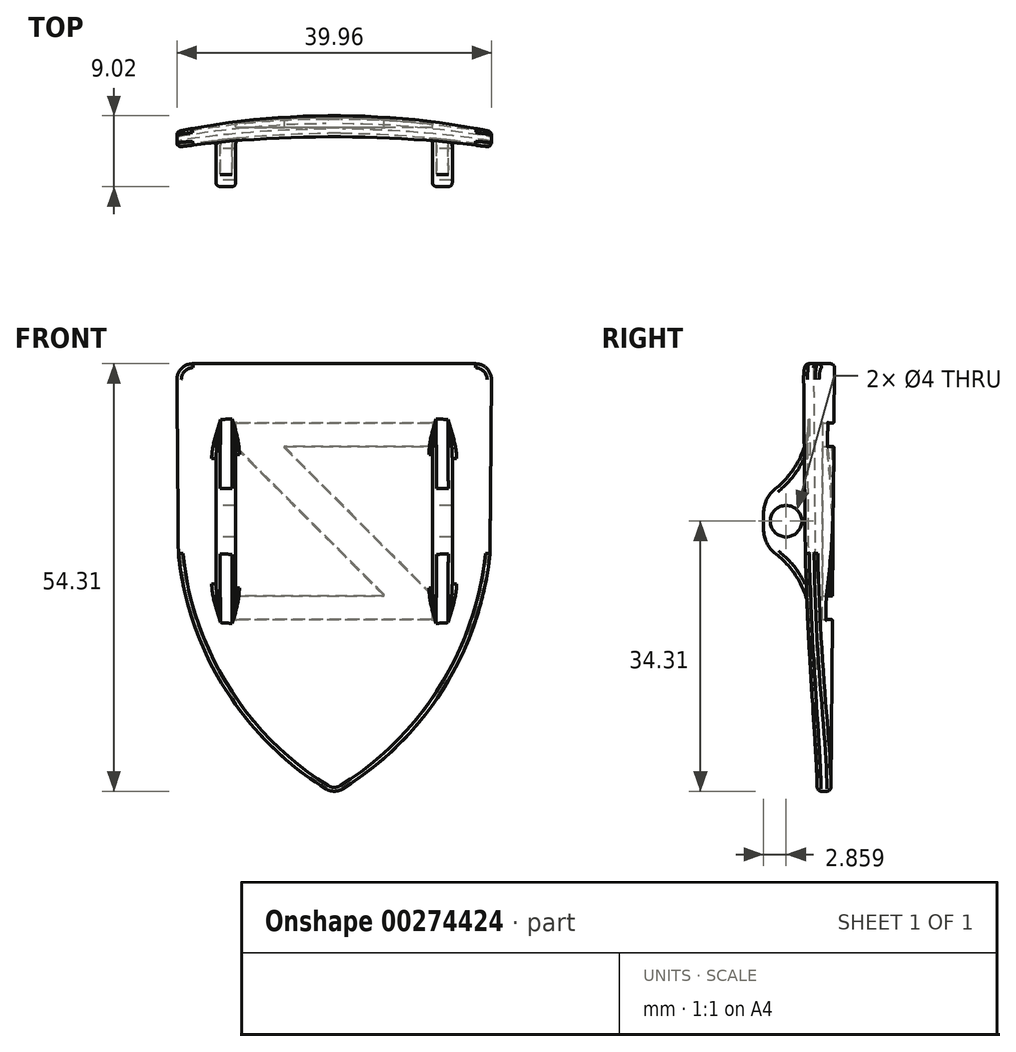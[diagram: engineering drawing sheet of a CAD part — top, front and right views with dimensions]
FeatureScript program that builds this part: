
annotation { "Feature Type Name" : "Feature", "Feature Type Description" : "" }
export const myFeature = defineFeature(function(context is Context, id is Id, definition is map)
    precondition{}
    {
        {
            var Q0;
            Q0=qCreatedBy(makeId("Top.planeOp"),FACE);
            var sketch = newSketch(context, id + "F0", { "sketchPlane" : qUnion([Q0])});
            skLineSegment(sketch, "E0", {"start": v(0, 0) * mm, "end": v(-20, 0) * mm});
            skLineSegment(sketch, "E1", {"start": v(0, 0) * mm, "end": v(20, 0) * mm});
            skArc(sketch, "E2", {"start": v(20, 0) * mm, "mid": v(0, 2.02) * mm, "end": v(-20, 0) * mm});
            skLineSegment(sketch, "E3", {"start": v(-20, 0) * mm, "end": v(-20, -2) * mm});
            skLineSegment(sketch, "E4", {"start": v(20, 0) * mm, "end": v(20, -2) * mm});
            skArc(sketch, "E5", {"start": v(20, -2) * mm, "mid": v(0, -0.66) * mm, "end": v(-20, -2) * mm});
            skSolve(sketch);
        }
        {
            var Q0;
            Q0=qCreatedBy(makeId("Front.planeOp"),FACE);
            var sketch = newSketch(context, id + "F1", { "sketchPlane" : qUnion([Q0])});
            skPoint(sketch, "E6.0", {"position": v(-20, 0) * mm});
            skPoint(sketch, "E7.0", {"position": v(20, 0) * mm});
            skLineSegment(sketch, "E8.bottom", {"start": v(-20, 0) * mm, "end": v(20, 0) * mm});
            skLineSegment(sketch, "E8.top", {"start": v(-20, -60) * mm, "end": v(20, -60) * mm});
            skLineSegment(sketch, "E8.left", {"start": v(-20, 0) * mm, "end": v(-20, -60) * mm});
            skLineSegment(sketch, "E8.right", {"start": v(20, 0) * mm, "end": v(20, -60) * mm});
            skPoint(sketch, "E9", {"position": v(-20, -20) * mm});
            skArc(sketch, "E10", {"start": v(20, -20) * mm, "mid": v(14.64, -40) * mm, "end": v(0, -54.64) * mm});
            skArc(sketch, "E11", {"start": v(-20, -20) * mm, "mid": v(-14.64, -40) * mm, "end": v(0, -54.64) * mm});
            skLineSegment(sketch, "E12.bottom", {"start": v(-12.5, -25) * mm, "end": v(12.5, -25) * mm});
            skLineSegment(sketch, "E12.top", {"start": v(-12.5, -15) * mm, "end": v(12.5, -15) * mm});
            skLineSegment(sketch, "E12.left", {"start": v(-12.5, -25) * mm, "end": v(-12.5, -15) * mm});
            skLineSegment(sketch, "E12.right", {"start": v(12.5, -25) * mm, "end": v(12.5, -15) * mm});
            skPoint(sketch, "E12.middle", {"position": v(0, -20) * mm});
            skLineSegment(sketch, "E13.bottom", {"start": v(-12.5, -25) * mm, "end": v(-15, -25) * mm});
            skLineSegment(sketch, "E13.top", {"start": v(-12.5, -15) * mm, "end": v(-15, -15) * mm});
            skLineSegment(sketch, "E13.right", {"start": v(-15, -25) * mm, "end": v(-15, -15) * mm});
            skLineSegment(sketch, "E14.MirrorCS", {"start": v(12.5, -15) * mm, "end": v(15, -15) * mm});
            skLineSegment(sketch, "E15.MirrorCS", {"start": v(15, -25) * mm, "end": v(15, -15) * mm});
            skLineSegment(sketch, "E16.MirrorCS", {"start": v(12.5, -25) * mm, "end": v(15, -25) * mm});
            skSolve(sketch);
        }
        {
            var Q0;
            Q0=makeQuery(id+"F0.imprint","IMPRINT",FACE,{"disambiguationData":[TD([[makeQuery(id+"F0.imprint","IMPRINT",EDGE,{"derivedFrom":sQuery(id+"F0.wireOp",EDGE,"E0")}),1.0]])]});
            var Q1;
            Q1=makeQuery(id+"F0.imprint","IMPRINT",FACE,{"disambiguationData":[TD([[makeQuery(id+"F0.imprint","IMPRINT",EDGE,{"derivedFrom":sQuery(id+"F0.wireOp",EDGE,"E0")}),-1.0]])]});
            extrude(context, id + "F2", {"entities" : qUnion([Q0, Q1]), "oppositeDirection" : true, "depth" : 60 * mm, "hasDraft" : true, "draftAngle" : 0.5 * degree, "draftPullDirection" : true});
        }
        {
            var Q0;
            {var subQ2=sQuery(id+"F1.wireOp",EDGE,"E8.top");Q0=makeQuery(id+"F1.imprint","IMPRINT",FACE,{"disambiguationData":[TD([[makeQuery(id+"F1.imprint","IMPRINT",EDGE,{"derivedFrom":subQ2}),1.0]])]});}
            extrude(context, id + "F3", {"entities" : qUnion([Q0]), "operationType" : NewBodyOperationType.REMOVE, "endBound" : BoundingType.SYMMETRIC, "depth" : 5 * mm});
        }
        {
            var Q0;
            Q0=makeQuery(id+"F1.imprint","IMPRINT",FACE,{"disambiguationData":[TD([[makeQuery(id+"F1.imprint","IMPRINT",EDGE,{"derivedFrom":sQuery(id+"F1.wireOp",EDGE,"E13.bottom")}),-1.0]])]});
            var Q1;
            Q1=makeQuery(id+"F1.imprint","IMPRINT",FACE,{"disambiguationData":[TD([[makeQuery(id+"F1.imprint","IMPRINT",EDGE,{"derivedFrom":sQuery(id+"F1.wireOp",EDGE,"E12.right")}),-1.0]])]});
            extrude(context, id + "F4", {"entities" : qUnion([Q0, Q1]), "operationType" : NewBodyOperationType.ADD, "depth" : 7 * mm});
        }
        {
            var Q0;
            Q0=makeQuery(id+"F4.opExtrude","SWEPT_FACE",FACE,{"disambiguationData":[OSD([sQuery(id+"F1.wireOp",EDGE,"E13.right")])]});
            var sketch = newSketch(context, id + "F5", { "sketchPlane" : qUnion([Q0])});
            skCircle(sketch, "E17", {"center": v(4.14, -20) * mm, "radius": 2 * mm});
            skPoint(sketch, "E17.centerSnap0", {"position": v(4.14, -15) * mm});
            skPoint(sketch, "E17.centerSnap1", {"position": v(7, -20) * mm});
            skSolve(sketch);
        }
        {
            var Q0;
            Q0=makeQuery(id+"F5.imprint","IMPRINT",FACE,{"disambiguationData":[TD([[makeQuery(id+"F5.imprint","IMPRINT",EDGE,{"derivedFrom":sQuery(id+"F5.wireOp",EDGE,"E17")}),1.0]])]});
            extrude(context, id + "F6", {"entities" : qUnion([Q0]), "operationType" : NewBodyOperationType.REMOVE, "oppositeDirection" : true, "depth" : 30 * mm});
        }
        {
            var Q0;
            Q0=makeQuery(id+"F4.opExtrude","CAP_EDGE",EDGE,{"disambiguationData":[OSD([sQuery(id+"F1.wireOp",EDGE,"E13.top")])],"isStart":false});
            var Q1;
            Q1=makeQuery(id+"F4.opExtrude","CAP_EDGE",EDGE,{"disambiguationData":[OSD([sQuery(id+"F1.wireOp",EDGE,"E13.bottom")])],"isStart":false});
            var Q2;
            Q2=makeQuery(id+"F4.opExtrude","CAP_EDGE",EDGE,{"disambiguationData":[OSD([sQuery(id+"F1.wireOp",EDGE,"E14.MirrorCS")])],"isStart":false});
            var Q3;
            Q3=makeQuery(id+"F4.opExtrude","CAP_EDGE",EDGE,{"disambiguationData":[OSD([sQuery(id+"F1.wireOp",EDGE,"E16.MirrorCS")])],"isStart":false});
            fillet(context, id + "F7", {"entities" : qUnion([Q0, Q1, Q2, Q3]), "radius" : 4 * mm, "tangentPropagation" : true, "allowEdgeOverflow" : false});
        }
        {
            var Q0;
            Q0=makeQuery(id+"F2.opExtrude","SWEPT_FACE",FACE,{"disambiguationData":[OSD([sQuery(id+"F0.wireOp",EDGE,"E2")])]});
            var Q1;
            Q1=makeQuery(id+"F2.opExtrude","CAP_EDGE",EDGE,{"disambiguationData":[OSD([sQuery(id+"F0.wireOp",EDGE,"E5")])],"isStart":true});
            var Q2;
            Q2=makeQuery(id+"F2.opExtrude","SWEPT_EDGE",EDGE,{"disambiguationData":[OSD([sQuery(id+"F0.wireOp",EDGE,"E3"),sQuery(id+"F0.wireOp",EDGE,"E5")])]});
            var Q3;
            Q3=makeQuery(id+"F3.boolean.opBoolean","INTERSECT",EDGE,{"derivedFrom":[makeQuery(id+"F2.opExtrude","SWEPT_FACE",FACE,{"disambiguationData":[OSD([sQuery(id+"F0.wireOp",EDGE,"E5")])]}),makeQuery(id+"F3.opExtrude","SWEPT_FACE",FACE,{"disambiguationData":[OSD([sQuery(id+"F1.wireOp",EDGE,"E11")])]})]});
            var Q4;
            Q4=makeQuery(id+"F2.opExtrude","SWEPT_EDGE",EDGE,{"disambiguationData":[OSD([sQuery(id+"F0.wireOp",EDGE,"E4"),sQuery(id+"F0.wireOp",EDGE,"E5")])]});
            var Q5;
            Q5=makeQuery(id+"F3.boolean.opBoolean","INTERSECT",EDGE,{"derivedFrom":[makeQuery(id+"F2.opExtrude","SWEPT_FACE",FACE,{"disambiguationData":[OSD([sQuery(id+"F0.wireOp",EDGE,"E5")])]}),makeQuery(id+"F3.opExtrude","SWEPT_FACE",FACE,{"disambiguationData":[OSD([sQuery(id+"F1.wireOp",EDGE,"E10")])]})]});
            fillet(context, id + "F8", {"entities" : qUnion([Q0, Q1, Q2, Q3, Q4, Q5]), "radius" : 0.5 * mm, "tangentPropagation" : true, "allowEdgeOverflow" : false});
        }
        {
            var Q0;
            Q0=makeQuery(id+"F2.opExtrude","CAP_EDGE",EDGE,{"disambiguationData":[OSD([sQuery(id+"F0.wireOp",EDGE,"E3")])],"isStart":true});
            var Q1;
            Q1=makeQuery(id+"F3.boolean.opBoolean","COPY",EDGE,{"derivedFrom":makeQuery(id+"F3.opExtrude","SWEPT_EDGE",EDGE,{"disambiguationData":[OSD([sQuery(id+"F1.wireOp",EDGE,"E10"),sQuery(id+"F1.wireOp",EDGE,"E11")])]})});
            var Q2;
            Q2=makeQuery(id+"F2.opExtrude","CAP_EDGE",EDGE,{"disambiguationData":[OSD([sQuery(id+"F0.wireOp",EDGE,"E4")])],"isStart":true});
            var Q3;
            Q3=makeQuery(id+"F3.boolean.opBoolean","INTERSECT",EDGE,{"derivedFrom":[makeQuery(id+"F2.opExtrude","SWEPT_FACE",FACE,{"disambiguationData":[OSD([sQuery(id+"F0.wireOp",EDGE,"E3")])]}),makeQuery(id+"F3.opExtrude","SWEPT_FACE",FACE,{"disambiguationData":[OSD([sQuery(id+"F1.wireOp",EDGE,"E11")])]})]});
            var Q4;
            Q4=makeQuery(id+"F3.boolean.opBoolean","INTERSECT",EDGE,{"derivedFrom":[makeQuery(id+"F2.opExtrude","SWEPT_FACE",FACE,{"disambiguationData":[OSD([sQuery(id+"F0.wireOp",EDGE,"E4")])]}),makeQuery(id+"F3.opExtrude","SWEPT_FACE",FACE,{"disambiguationData":[OSD([sQuery(id+"F1.wireOp",EDGE,"E10")])]})]});
            fillet(context, id + "F9", {"entities" : qUnion([Q0, Q1, Q2, Q3, Q4]), "radius" : 2 * mm, "tangentPropagation" : true, "allowEdgeOverflow" : false});
        }
        {
            var Q0;
            Q0=makeQuery(id+"F6.boolean.opBoolean","COPY",FACE,{"disambiguationData":[TD([makeQuery(id+"F4.opExtrude","SWEPT_FACE",FACE,{"disambiguationData":[OSD([sQuery(id+"F1.wireOp",EDGE,"E12.left")])]})])],"derivedFrom":makeQuery(id+"F6.opExtrude","SWEPT_FACE",FACE,{"disambiguationData":[OSD([sQuery(id+"F5.wireOp",EDGE,"E17")])]})});
            var Q1;
            Q1=makeQuery(id+"F6.boolean.opBoolean","COPY",FACE,{"disambiguationData":[TD([makeQuery(id+"F4.opExtrude","SWEPT_FACE",FACE,{"disambiguationData":[OSD([sQuery(id+"F1.wireOp",EDGE,"E12.right")])]})])],"derivedFrom":makeQuery(id+"F6.opExtrude","SWEPT_FACE",FACE,{"disambiguationData":[OSD([sQuery(id+"F5.wireOp",EDGE,"E17")])]})});
            fillet(context, id + "F10", {"entities" : qUnion([Q0, Q1]), "radius" : 0.1 * mm, "tangentPropagation" : true, "allowEdgeOverflow" : false});
        }
        {
            var Q0;
            Q0=qCreatedBy(makeId("Front.planeOp"),FACE);
            cPlane(context, id + "F11", {"entities" : qUnion([Q0]), "cplaneType" : CPlaneType.OFFSET, "offset" : 10 * mm, "oppositeDirection" : true, "width" : 150 * mm, "height" : 150 * mm});
        }
        {
            var Q0;
            Q0=qCreatedBy(id+"F11.planeOp",FACE);
            var sketch = newSketch(context, id + "F12", { "sketchPlane" : qUnion([Q0])});
            skPoint(sketch, "E18.0", {"position": v(0, -20) * mm});
            skPoint(sketch, "E19.0", {"position": v(-12.5, -15) * mm});
            skPoint(sketch, "E20.0", {"position": v(12.5, -15) * mm});
            skLineSegment(sketch, "E21.bottom", {"start": v(-12.5, -7.5) * mm, "end": v(12.5, -7.5) * mm, "construction": true});
            skLineSegment(sketch, "E21.top", {"start": v(-12.5, -32.5) * mm, "end": v(12.5, -32.5) * mm, "construction": true});
            skLineSegment(sketch, "E21.left", {"start": v(-12.5, -7.5) * mm, "end": v(-12.5, -32.5) * mm, "construction": true});
            skLineSegment(sketch, "E21.right", {"start": v(12.5, -7.5) * mm, "end": v(12.5, -32.5) * mm, "construction": true});
            skLineSegment(sketch, "E22", {"start": v(9.5, -29.5) * mm, "end": v(-9.5, -10.5) * mm, "construction": true});
            skLineSegment(sketch, "E23.bottom", {"start": v(12.5, -7.5) * mm, "end": v(-12.5, -7.5) * mm});
            skLineSegment(sketch, "E23.top", {"start": v(12.5, -10.5) * mm, "end": v(-6.5, -10.5) * mm});
            skLineSegment(sketch, "E23.left", {"start": v(12.5, -7.5) * mm, "end": v(12.5, -10.5) * mm});
            skLineSegment(sketch, "E23.right", {"start": v(-12.5, -7.5) * mm, "end": v(-12.5, -10.5) * mm});
            skLineSegment(sketch, "E24.bottom", {"start": v(12.5, -32.5) * mm, "end": v(-12.5, -32.5) * mm});
            skLineSegment(sketch, "E24.left", {"start": v(12.5, -32.5) * mm, "end": v(12.5, -29.5) * mm});
            skLineSegment(sketch, "E24.right", {"start": v(-12.5, -32.5) * mm, "end": v(-12.5, -29.5) * mm});
            skLineSegment(sketch, "E25", {"start": v(12.5, -29.5) * mm, "end": v(-6.5, -10.5) * mm});
            skLineSegment(sketch, "E26", {"start": v(-12.5, -10.5) * mm, "end": v(6.5, -29.5) * mm});
            skLineSegment(sketch, "E27.trimOffspring", {"start": v(6.5, -29.5) * mm, "end": v(-12.5, -29.5) * mm});
            skSolve(sketch);
        }
        {
            var Q0;
            Q0=makeQuery(id+"F12.imprint","IMPRINT",FACE,{"disambiguationData":[TD([[makeQuery(id+"F12.imprint","IMPRINT",EDGE,{"derivedFrom":sQuery(id+"F12.wireOp",EDGE,"E23.bottom")}),1.0]])]});
            extrude(context, id + "F13", {"entities" : qUnion([Q0]), "operationType" : NewBodyOperationType.REMOVE, "depth" : 9.5 * mm});
        }
        {
            var Q0;
            Q0=makeQuery(id+"F13.boolean.opBoolean","INTERSECT",EDGE,{"derivedFrom":[makeQuery(id+"F2.opExtrude","SWEPT_FACE",FACE,{"disambiguationData":[OSD([sQuery(id+"F0.wireOp",EDGE,"E2")])]}),makeQuery(id+"F13.opExtrude","SWEPT_FACE",FACE,{"disambiguationData":[OSD([sQuery(id+"F12.wireOp",EDGE,"E23.top")])]})]});
            var Q1;
            Q1=makeQuery(id+"F13.boolean.opBoolean","INTERSECT",EDGE,{"derivedFrom":[makeQuery(id+"F2.opExtrude","SWEPT_FACE",FACE,{"disambiguationData":[OSD([sQuery(id+"F0.wireOp",EDGE,"E2")])]}),makeQuery(id+"F13.opExtrude","SWEPT_FACE",FACE,{"disambiguationData":[OSD([sQuery(id+"F12.wireOp",EDGE,"E23.left")])]})]});
            var Q2;
            Q2=makeQuery(id+"F13.boolean.opBoolean","INTERSECT",EDGE,{"derivedFrom":[makeQuery(id+"F2.opExtrude","SWEPT_FACE",FACE,{"disambiguationData":[OSD([sQuery(id+"F0.wireOp",EDGE,"E2")])]}),makeQuery(id+"F13.opExtrude","SWEPT_FACE",FACE,{"disambiguationData":[OSD([sQuery(id+"F12.wireOp",EDGE,"E23.bottom")])]})]});
            var Q3;
            Q3=makeQuery(id+"F13.boolean.opBoolean","INTERSECT",EDGE,{"derivedFrom":[makeQuery(id+"F2.opExtrude","SWEPT_FACE",FACE,{"disambiguationData":[OSD([sQuery(id+"F0.wireOp",EDGE,"E2")])]}),makeQuery(id+"F13.opExtrude","SWEPT_FACE",FACE,{"disambiguationData":[OSD([sQuery(id+"F12.wireOp",EDGE,"E23.right")])]})]});
            var Q4;
            Q4=makeQuery(id+"F13.boolean.opBoolean","INTERSECT",EDGE,{"derivedFrom":[makeQuery(id+"F2.opExtrude","SWEPT_FACE",FACE,{"disambiguationData":[OSD([sQuery(id+"F0.wireOp",EDGE,"E2")])]}),makeQuery(id+"F13.opExtrude","SWEPT_FACE",FACE,{"disambiguationData":[OSD([sQuery(id+"F12.wireOp",EDGE,"E26")])]})]});
            var Q5;
            Q5=makeQuery(id+"F13.boolean.opBoolean","INTERSECT",EDGE,{"derivedFrom":[makeQuery(id+"F2.opExtrude","SWEPT_FACE",FACE,{"disambiguationData":[OSD([sQuery(id+"F0.wireOp",EDGE,"E2")])]}),makeQuery(id+"F13.opExtrude","SWEPT_FACE",FACE,{"disambiguationData":[OSD([sQuery(id+"F12.wireOp",EDGE,"E27.trimOffspring")])]})]});
            var Q6;
            Q6=makeQuery(id+"F13.boolean.opBoolean","INTERSECT",EDGE,{"derivedFrom":[makeQuery(id+"F2.opExtrude","SWEPT_FACE",FACE,{"disambiguationData":[OSD([sQuery(id+"F0.wireOp",EDGE,"E2")])]}),makeQuery(id+"F13.opExtrude","SWEPT_FACE",FACE,{"disambiguationData":[OSD([sQuery(id+"F12.wireOp",EDGE,"E24.bottom")])]})]});
            var Q7;
            Q7=makeQuery(id+"F13.boolean.opBoolean","INTERSECT",EDGE,{"derivedFrom":[makeQuery(id+"F2.opExtrude","SWEPT_FACE",FACE,{"disambiguationData":[OSD([sQuery(id+"F0.wireOp",EDGE,"E2")])]}),makeQuery(id+"F13.opExtrude","SWEPT_FACE",FACE,{"disambiguationData":[OSD([sQuery(id+"F12.wireOp",EDGE,"E24.right")])]})]});
            var Q8;
            Q8=makeQuery(id+"F13.boolean.opBoolean","INTERSECT",EDGE,{"derivedFrom":[makeQuery(id+"F2.opExtrude","SWEPT_FACE",FACE,{"disambiguationData":[OSD([sQuery(id+"F0.wireOp",EDGE,"E2")])]}),makeQuery(id+"F13.opExtrude","SWEPT_FACE",FACE,{"disambiguationData":[OSD([sQuery(id+"F12.wireOp",EDGE,"E24.left")])]})]});
            var Q9;
            Q9=makeQuery(id+"F13.boolean.opBoolean","INTERSECT",EDGE,{"derivedFrom":[makeQuery(id+"F2.opExtrude","SWEPT_FACE",FACE,{"disambiguationData":[OSD([sQuery(id+"F0.wireOp",EDGE,"E2")])]}),makeQuery(id+"F13.opExtrude","SWEPT_FACE",FACE,{"disambiguationData":[OSD([sQuery(id+"F12.wireOp",EDGE,"E25")])]})]});
            var Q10;
            Q10=makeQuery(id+"F13.boolean.opBoolean","COPY",EDGE,{"derivedFrom":makeQuery(id+"F13.opExtrude","SWEPT_EDGE",EDGE,{"disambiguationData":[OSD([sQuery(id+"F12.wireOp",EDGE,"E23.top"),sQuery(id+"F12.wireOp",EDGE,"E25")])]})});
            var Q11;
            Q11=makeQuery(id+"F13.boolean.opBoolean","COPY",EDGE,{"derivedFrom":makeQuery(id+"F13.opExtrude","SWEPT_EDGE",EDGE,{"disambiguationData":[OSD([sQuery(id+"F12.wireOp",EDGE,"E26"),sQuery(id+"F12.wireOp",EDGE,"E27.trimOffspring")])]})});
            var Q12;
            Q12=makeQuery(id+"F13.boolean.opBoolean","COPY",EDGE,{"derivedFrom":makeQuery(id+"F13.opExtrude","SWEPT_EDGE",EDGE,{"disambiguationData":[OSD([sQuery(id+"F12.wireOp",EDGE,"E23.bottom"),sQuery(id+"F12.wireOp",EDGE,"E23.right")])]})});
            var Q13;
            Q13=makeQuery(id+"F13.boolean.opBoolean","COPY",EDGE,{"derivedFrom":makeQuery(id+"F13.opExtrude","SWEPT_EDGE",EDGE,{"disambiguationData":[OSD([sQuery(id+"F12.wireOp",EDGE,"E23.right"),sQuery(id+"F12.wireOp",EDGE,"E26")])]})});
            var Q14;
            Q14=makeQuery(id+"F13.boolean.opBoolean","COPY",EDGE,{"derivedFrom":makeQuery(id+"F13.opExtrude","SWEPT_EDGE",EDGE,{"disambiguationData":[OSD([sQuery(id+"F12.wireOp",EDGE,"E23.top"),sQuery(id+"F12.wireOp",EDGE,"E23.left")])]})});
            var Q15;
            Q15=makeQuery(id+"F13.boolean.opBoolean","COPY",EDGE,{"derivedFrom":makeQuery(id+"F13.opExtrude","SWEPT_EDGE",EDGE,{"disambiguationData":[OSD([sQuery(id+"F12.wireOp",EDGE,"E23.bottom"),sQuery(id+"F12.wireOp",EDGE,"E23.left")])]})});
            var Q16;
            Q16=makeQuery(id+"F13.boolean.opBoolean","COPY",EDGE,{"derivedFrom":makeQuery(id+"F13.opExtrude","SWEPT_EDGE",EDGE,{"disambiguationData":[OSD([sQuery(id+"F12.wireOp",EDGE,"E24.bottom"),sQuery(id+"F12.wireOp",EDGE,"E24.left")])]})});
            var Q17;
            Q17=makeQuery(id+"F13.boolean.opBoolean","COPY",EDGE,{"derivedFrom":makeQuery(id+"F13.opExtrude","SWEPT_EDGE",EDGE,{"disambiguationData":[OSD([sQuery(id+"F12.wireOp",EDGE,"E24.left"),sQuery(id+"F12.wireOp",EDGE,"E25")])]})});
            var Q18;
            Q18=makeQuery(id+"F13.boolean.opBoolean","COPY",EDGE,{"derivedFrom":makeQuery(id+"F13.opExtrude","SWEPT_EDGE",EDGE,{"disambiguationData":[OSD([sQuery(id+"F12.wireOp",EDGE,"E24.bottom"),sQuery(id+"F12.wireOp",EDGE,"E24.right")])]})});
            var Q19;
            Q19=makeQuery(id+"F13.boolean.opBoolean","COPY",EDGE,{"derivedFrom":makeQuery(id+"F13.opExtrude","SWEPT_EDGE",EDGE,{"disambiguationData":[OSD([sQuery(id+"F12.wireOp",EDGE,"E24.right"),sQuery(id+"F12.wireOp",EDGE,"E27.trimOffspring")])]})});
            var Q20;
            Q20=makeQuery(id+"F13.boolean.opBoolean","COPY",FACE,{"derivedFrom":makeQuery(id+"F13.opExtrude","CAP_FACE",FACE,{"disambiguationData":[OSD([sQuery(id+"F12.wireOp",EDGE,"E23.bottom"),sQuery(id+"F12.wireOp",EDGE,"E23.top"),sQuery(id+"F12.wireOp",EDGE,"E23.left"),sQuery(id+"F12.wireOp",EDGE,"E23.right"),sQuery(id+"F12.wireOp",EDGE,"E24.bottom"),sQuery(id+"F12.wireOp",EDGE,"E24.left"),sQuery(id+"F12.wireOp",EDGE,"E24.right"),sQuery(id+"F12.wireOp",EDGE,"E25"),sQuery(id+"F12.wireOp",EDGE,"E26"),sQuery(id+"F12.wireOp",EDGE,"E27.trimOffspring")])],"isStart":false})});
            fillet(context, id + "F14", {"entities" : qUnion([Q0, Q1, Q2, Q3, Q4, Q5, Q6, Q7, Q8, Q9, Q10, Q11, Q12, Q13, Q14, Q15, Q16, Q17, Q18, Q19, Q20]), "radius" : 0.1 * mm, "tangentPropagation" : true, "allowEdgeOverflow" : false});
        }
        {
            var Q0;
            Q0=makeQuery(id+"F4.boolean.opBoolean","INTERSECT",EDGE,{"derivedFrom":[makeQuery(id+"F2.opExtrude","SWEPT_FACE",FACE,{"disambiguationData":[OSD([sQuery(id+"F0.wireOp",EDGE,"E5")])]}),makeQuery(id+"F4.opExtrude","SWEPT_FACE",FACE,{"disambiguationData":[OSD([sQuery(id+"F1.wireOp",EDGE,"E13.top")])]})]});
            var Q1;
            Q1=makeQuery(id+"F4.boolean.opBoolean","INTERSECT",EDGE,{"derivedFrom":[makeQuery(id+"F2.opExtrude","SWEPT_FACE",FACE,{"disambiguationData":[OSD([sQuery(id+"F0.wireOp",EDGE,"E5")])]}),makeQuery(id+"F4.opExtrude","SWEPT_FACE",FACE,{"disambiguationData":[OSD([sQuery(id+"F1.wireOp",EDGE,"E14.MirrorCS")])]})]});
            var Q2;
            Q2=makeQuery(id+"F4.boolean.opBoolean","INTERSECT",EDGE,{"derivedFrom":[makeQuery(id+"F2.opExtrude","SWEPT_FACE",FACE,{"disambiguationData":[OSD([sQuery(id+"F0.wireOp",EDGE,"E5")])]}),makeQuery(id+"F4.opExtrude","SWEPT_FACE",FACE,{"disambiguationData":[OSD([sQuery(id+"F1.wireOp",EDGE,"E16.MirrorCS")])]})]});
            var Q3;
            Q3=makeQuery(id+"F4.boolean.opBoolean","INTERSECT",EDGE,{"derivedFrom":[makeQuery(id+"F2.opExtrude","SWEPT_FACE",FACE,{"disambiguationData":[OSD([sQuery(id+"F0.wireOp",EDGE,"E5")])]}),makeQuery(id+"F4.opExtrude","SWEPT_FACE",FACE,{"disambiguationData":[OSD([sQuery(id+"F1.wireOp",EDGE,"E13.bottom")])]})]});
            fillet(context, id + "F15", {"entities" : qUnion([Q0, Q1, Q2, Q3]), "radius" : 11 * mm, "tangentPropagation" : true, "allowEdgeOverflow" : false});
        }
        {
            var Q0;
            Q0=makeQuery(id+"F15.opFillet","BLEND_EDGE",EDGE,{"blendedFrom":[makeQuery(id+"F4.boolean.opBoolean","INTERSECT",EDGE,{"derivedFrom":[makeQuery(id+"F2.opExtrude","SWEPT_FACE",FACE,{"disambiguationData":[OSD([sQuery(id+"F0.wireOp",EDGE,"E5")])]}),makeQuery(id+"F4.opExtrude","SWEPT_FACE",FACE,{"disambiguationData":[OSD([sQuery(id+"F1.wireOp",EDGE,"E13.top")])]})]}),makeQuery(id+"F4.opExtrude","SWEPT_FACE",FACE,{"disambiguationData":[OSD([sQuery(id+"F1.wireOp",EDGE,"E12.left")])]})],"blendedInto":[makeQuery(id+"F4.opExtrude","SWEPT_FACE",FACE,{"disambiguationData":[OSD([sQuery(id+"F1.wireOp",EDGE,"E12.left")])]})]});
            var Q1;
            Q1=makeQuery(id+"F15.opFillet","BLEND_EDGE",EDGE,{"blendedFrom":[makeQuery(id+"F4.boolean.opBoolean","INTERSECT",EDGE,{"derivedFrom":[makeQuery(id+"F2.opExtrude","SWEPT_FACE",FACE,{"disambiguationData":[OSD([sQuery(id+"F0.wireOp",EDGE,"E5")])]}),makeQuery(id+"F4.opExtrude","SWEPT_FACE",FACE,{"disambiguationData":[OSD([sQuery(id+"F1.wireOp",EDGE,"E13.top")])]})]}),makeQuery(id+"F4.opExtrude","SWEPT_FACE",FACE,{"disambiguationData":[OSD([sQuery(id+"F1.wireOp",EDGE,"E13.right")])]})],"blendedInto":[makeQuery(id+"F4.opExtrude","SWEPT_FACE",FACE,{"disambiguationData":[OSD([sQuery(id+"F1.wireOp",EDGE,"E13.right")])]})]});
            var Q2;
            Q2=makeQuery(id+"F15.opFillet","BLEND_EDGE",EDGE,{"blendedFrom":[makeQuery(id+"F4.boolean.opBoolean","INTERSECT",EDGE,{"derivedFrom":[makeQuery(id+"F2.opExtrude","SWEPT_FACE",FACE,{"disambiguationData":[OSD([sQuery(id+"F0.wireOp",EDGE,"E5")])]}),makeQuery(id+"F4.opExtrude","SWEPT_FACE",FACE,{"disambiguationData":[OSD([sQuery(id+"F1.wireOp",EDGE,"E14.MirrorCS")])]})]}),makeQuery(id+"F4.opExtrude","SWEPT_FACE",FACE,{"disambiguationData":[OSD([sQuery(id+"F1.wireOp",EDGE,"E12.right")])]})],"blendedInto":[makeQuery(id+"F4.opExtrude","SWEPT_FACE",FACE,{"disambiguationData":[OSD([sQuery(id+"F1.wireOp",EDGE,"E12.right")])]})]});
            var Q3;
            Q3=makeQuery(id+"F15.opFillet","BLEND_EDGE",EDGE,{"blendedFrom":[makeQuery(id+"F4.boolean.opBoolean","INTERSECT",EDGE,{"derivedFrom":[makeQuery(id+"F2.opExtrude","SWEPT_FACE",FACE,{"disambiguationData":[OSD([sQuery(id+"F0.wireOp",EDGE,"E5")])]}),makeQuery(id+"F4.opExtrude","SWEPT_FACE",FACE,{"disambiguationData":[OSD([sQuery(id+"F1.wireOp",EDGE,"E14.MirrorCS")])]})]}),makeQuery(id+"F4.opExtrude","SWEPT_FACE",FACE,{"disambiguationData":[OSD([sQuery(id+"F1.wireOp",EDGE,"E15.MirrorCS")])]})],"blendedInto":[makeQuery(id+"F4.opExtrude","SWEPT_FACE",FACE,{"disambiguationData":[OSD([sQuery(id+"F1.wireOp",EDGE,"E15.MirrorCS")])]})]});
            var Q4;
            Q4=makeQuery(id+"F4.boolean.opBoolean","INTERSECT",EDGE,{"derivedFrom":[makeQuery(id+"F2.opExtrude","SWEPT_FACE",FACE,{"disambiguationData":[OSD([sQuery(id+"F0.wireOp",EDGE,"E5")])]}),makeQuery(id+"F4.opExtrude","SWEPT_FACE",FACE,{"disambiguationData":[OSD([sQuery(id+"F1.wireOp",EDGE,"E15.MirrorCS")])]})]});
            var Q5;
            Q5=makeQuery(id+"F4.boolean.opBoolean","INTERSECT",EDGE,{"derivedFrom":[makeQuery(id+"F2.opExtrude","SWEPT_FACE",FACE,{"disambiguationData":[OSD([sQuery(id+"F0.wireOp",EDGE,"E5")])]}),makeQuery(id+"F4.opExtrude","SWEPT_FACE",FACE,{"disambiguationData":[OSD([sQuery(id+"F1.wireOp",EDGE,"E12.left")])]})]});
            var Q6;
            Q6=makeQuery(id+"F4.boolean.opBoolean","INTERSECT",EDGE,{"derivedFrom":[makeQuery(id+"F2.opExtrude","SWEPT_FACE",FACE,{"disambiguationData":[OSD([sQuery(id+"F0.wireOp",EDGE,"E5")])]}),makeQuery(id+"F4.opExtrude","SWEPT_FACE",FACE,{"disambiguationData":[OSD([sQuery(id+"F1.wireOp",EDGE,"E12.right")])]})]});
            var Q7;
            Q7=makeQuery(id+"F4.boolean.opBoolean","INTERSECT",EDGE,{"derivedFrom":[makeQuery(id+"F2.opExtrude","SWEPT_FACE",FACE,{"disambiguationData":[OSD([sQuery(id+"F0.wireOp",EDGE,"E5")])]}),makeQuery(id+"F4.opExtrude","SWEPT_FACE",FACE,{"disambiguationData":[OSD([sQuery(id+"F1.wireOp",EDGE,"E13.right")])]})]});
            fillet(context, id + "F16", {"entities" : qUnion([Q0, Q1, Q2, Q3, Q4, Q5, Q6, Q7]), "radius" : 0.5 * mm, "tangentPropagation" : true, "allowEdgeOverflow" : false});
        }
    });
